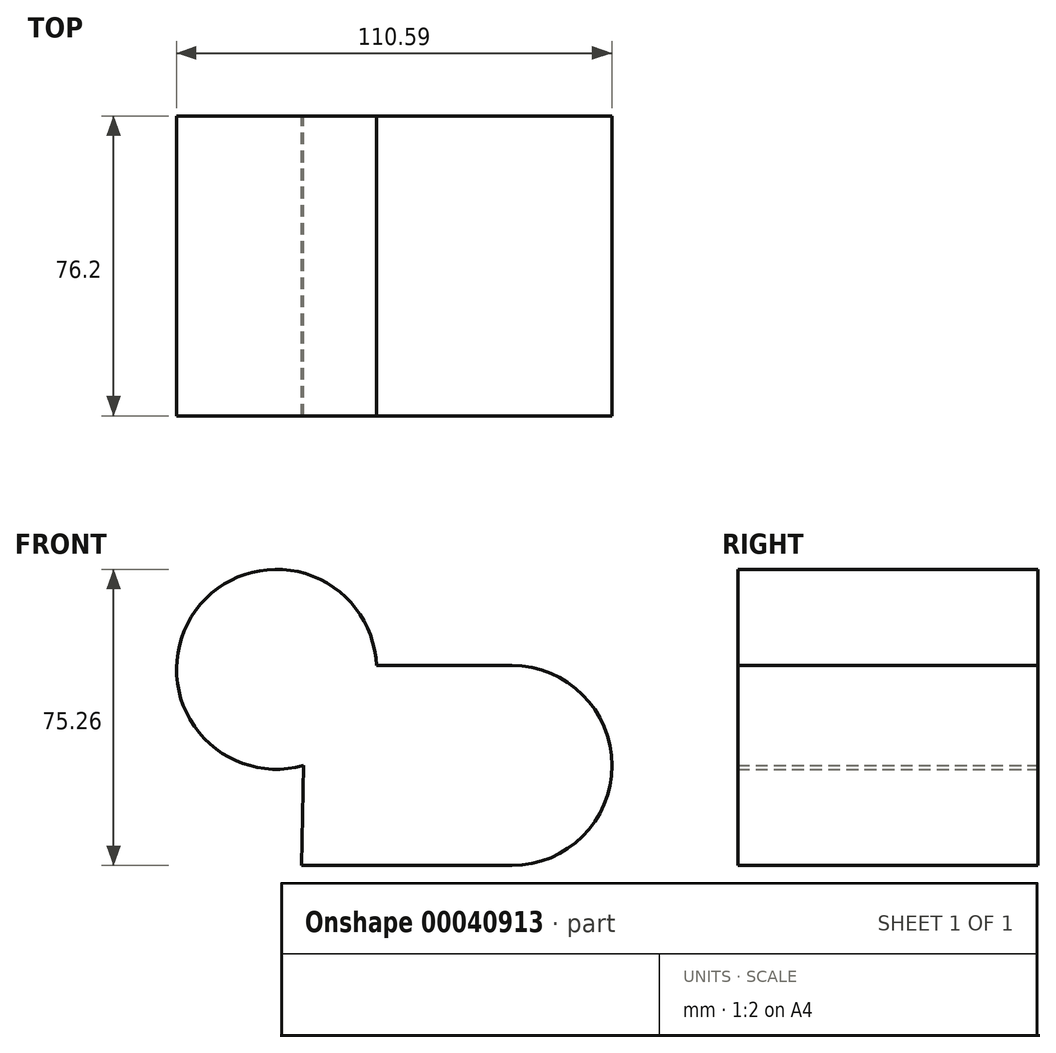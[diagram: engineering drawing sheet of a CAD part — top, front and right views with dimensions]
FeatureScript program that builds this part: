
annotation { "Feature Type Name" : "Feature", "Feature Type Description" : "" }
export const myFeature = defineFeature(function(context is Context, id is Id, definition is map)
    precondition{}
    {
        {
            var Q0;
            Q0=qCreatedBy(makeId("Front.planeOp"),FACE);
            var sketch = newSketch(context, id + "F0", { "sketchPlane" : qUnion([Q0])});
            skArc(sketch, "E0", {"start": v(-21.7, 19.62) * mm, "mid": v(-67.6, 33.66) * mm, "end": v(-40.25, -5.78) * mm});
            skLineSegment(sketch, "E1.bottom", {"start": v(12.71, 19.62) * mm, "end": v(-21.7, 19.62) * mm});
            skLineSegment(sketch, "E1.top", {"start": v(12.71, -31.18) * mm, "end": v(-40.73, -31.18) * mm});
            skLineSegment(sketch, "E1.right", {"start": v(-40.25, -5.78) * mm, "end": v(-40.73, -31.18) * mm});
            skArc(sketch, "E2", {"start": v(12.71, -31.18) * mm, "mid": v(38.11, -5.78) * mm, "end": v(12.71, 19.62) * mm});
            skSolve(sketch);
        }
        {
            var Q0;
            Q0=makeQuery(id+"F0.imprint","IMPRINT",FACE,{"disambiguationData":[TD([[makeQuery(id+"F0.imprint","IMPRINT",EDGE,{"derivedFrom":sQuery(id+"F0.wireOp",EDGE,"E0")}),1.0]])]});
            extrude(context, id + "F1", {"entities" : qUnion([Q0]), "depth" : 76.2 * mm});
        }
    });
